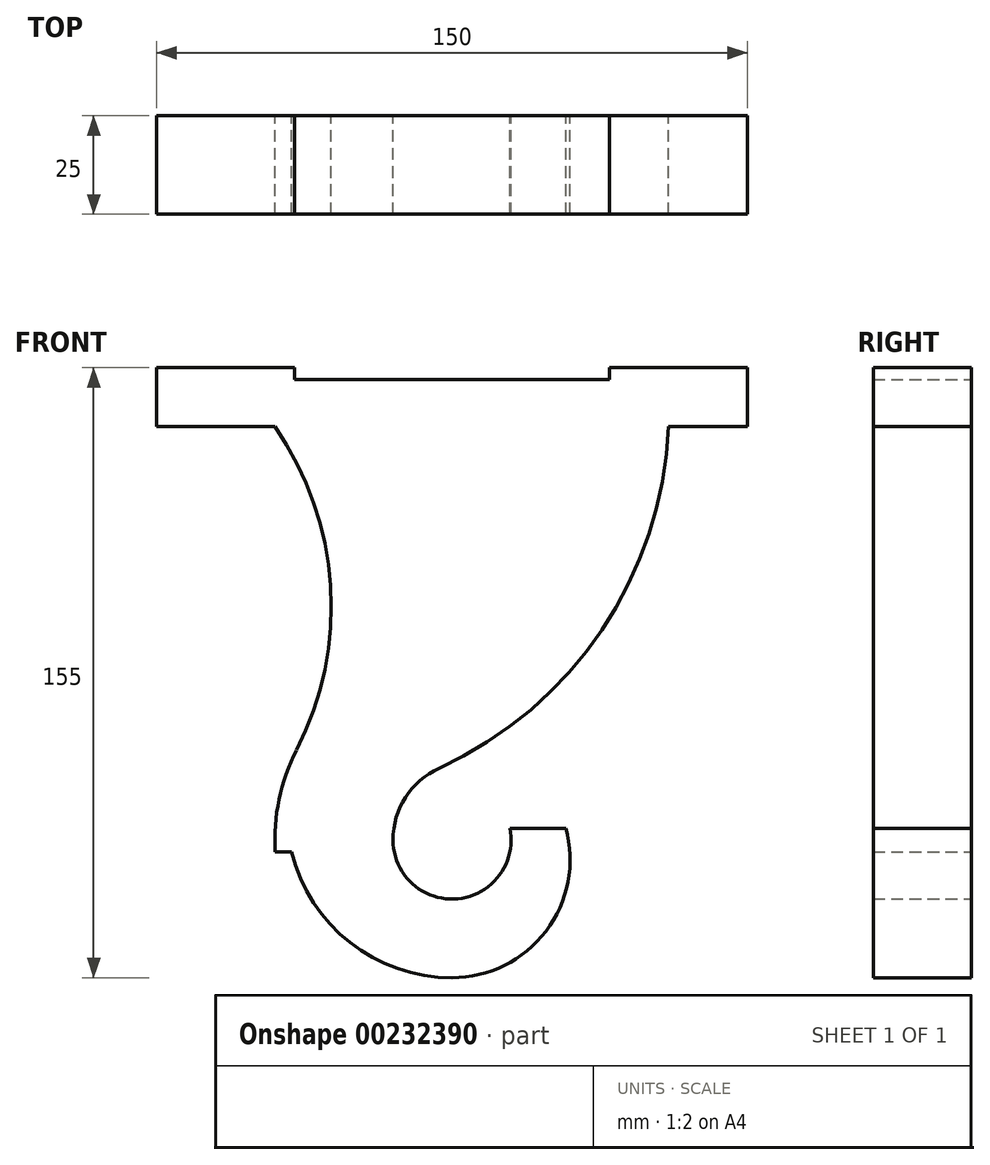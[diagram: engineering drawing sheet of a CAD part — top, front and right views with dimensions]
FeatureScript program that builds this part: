
annotation { "Feature Type Name" : "Feature", "Feature Type Description" : "" }
export const myFeature = defineFeature(function(context is Context, id is Id, definition is map)
    precondition{}
    {
        {
            var Q0;
            Q0=qCreatedBy(makeId("Front.planeOp"),FACE);
            var sketch = newSketch(context, id + "F0", { "sketchPlane" : qUnion([Q0])});
            skLineSegment(sketch, "E0", {"start": v(55, 105) * mm, "end": v(75, 105) * mm});
            skLineSegment(sketch, "E1", {"start": v(75, 105) * mm, "end": v(75, 120) * mm});
            skLineSegment(sketch, "E2", {"start": v(75, 120) * mm, "end": v(40, 120) * mm});
            skLineSegment(sketch, "E3", {"start": v(40, 120) * mm, "end": v(40, 117) * mm});
            skLineSegment(sketch, "E4", {"start": v(40, 117) * mm, "end": v(-40, 117) * mm});
            skLineSegment(sketch, "E5", {"start": v(-40, 117) * mm, "end": v(-40, 120) * mm});
            skLineSegment(sketch, "E6", {"start": v(-40, 120) * mm, "end": v(-75, 120) * mm});
            skLineSegment(sketch, "E7", {"start": v(-75, 120) * mm, "end": v(-75, 105) * mm});
            skLineSegment(sketch, "E8", {"start": v(-75, 105) * mm, "end": v(-45, 105) * mm});
            skArc(sketch, "E9", {"start": v(0, -35) * mm, "mid": v(23.87, -23.17) * mm, "end": v(28.91, 3) * mm});
            skArc(sketch, "E10", {"start": v(-15, 0) * mm, "mid": v(1.5, -14.92) * mm, "end": v(14.7, 3) * mm});
            skLineSegment(sketch, "E11", {"start": v(14.7, 3) * mm, "end": v(28.91, 3) * mm});
            skArc(sketch, "E12", {"start": v(-3.32, 18.19) * mm, "mid": v(-11.83, 10.8) * mm, "end": v(-15, 0) * mm});
            skArc(sketch, "E13", {"start": v(-3.32, 18.19) * mm, "mid": v(38.1, 53.36) * mm, "end": v(55, 105) * mm});
            skArc(sketch, "E14", {"start": v(-39.5, 22.82) * mm, "mid": v(-30.86, 64.67) * mm, "end": v(-45, 105) * mm});
            skLineSegment(sketch, "E15", {"start": v(-44.9, -3) * mm, "end": v(-40.8, -3) * mm});
            skArc(sketch, "E16", {"start": v(-44.9, -3) * mm, "mid": v(-43.93, 10.27) * mm, "end": v(-39.5, 22.82) * mm});
            skArc(sketch, "E17.trimOffspring", {"start": v(-40.8, -3) * mm, "mid": v(-25.92, -26.05) * mm, "end": v(0, -35) * mm});
            skSolve(sketch);
        }
        {
            var Q0;
            Q0=makeQuery(id+"F0.imprint","IMPRINT",FACE,{"disambiguationData":[TD([[makeQuery(id+"F0.imprint","IMPRINT",EDGE,{"derivedFrom":sQuery(id+"F0.wireOp",EDGE,"E0")}),1.0]])]});
            extrude(context, id + "F1", {"entities" : qUnion([Q0]), "depth" : 25 * mm});
        }
    });
